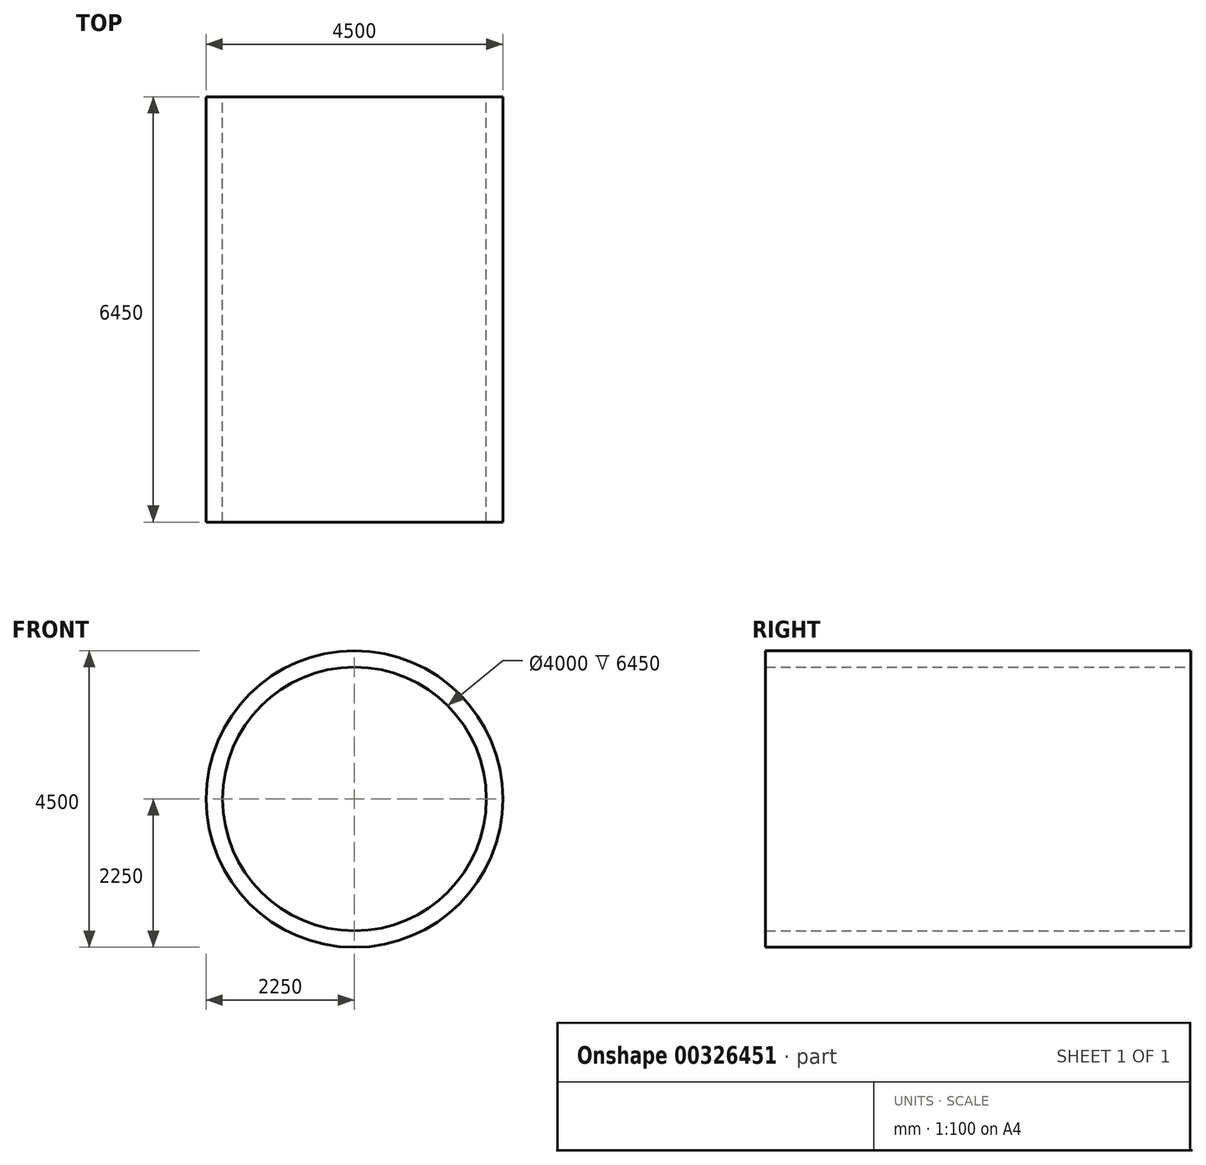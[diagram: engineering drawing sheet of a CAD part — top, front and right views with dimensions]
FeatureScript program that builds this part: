
annotation { "Feature Type Name" : "Feature", "Feature Type Description" : "" }
export const myFeature = defineFeature(function(context is Context, id is Id, definition is map)
    precondition{}
    {
        {
            var Q0;
            Q0=qCreatedBy(makeId("Front.planeOp"),FACE);
            var sketch = newSketch(context, id + "F0", { "sketchPlane" : qUnion([Q0])});
            skCircle(sketch, "E0", {"center": v(0, 0) * mm, "radius": 2000 * mm});
            skCircle(sketch, "E1.0", {"center": v(0, 0) * mm, "radius": 2250 * mm});
            skSolve(sketch);
        }
        {
            var Q0;
            Q0=makeQuery(id+"F0.imprint","IMPRINT",FACE,{"disambiguationData":[TD([[makeQuery(id+"F0.imprint","IMPRINT",EDGE,{"derivedFrom":sQuery(id+"F0.wireOp",EDGE,"E0")}),-1.0]])]});
            extrude(context, id + "F1", {"entities" : qUnion([Q0]), "depth" : 6450 * mm});
        }
    });
